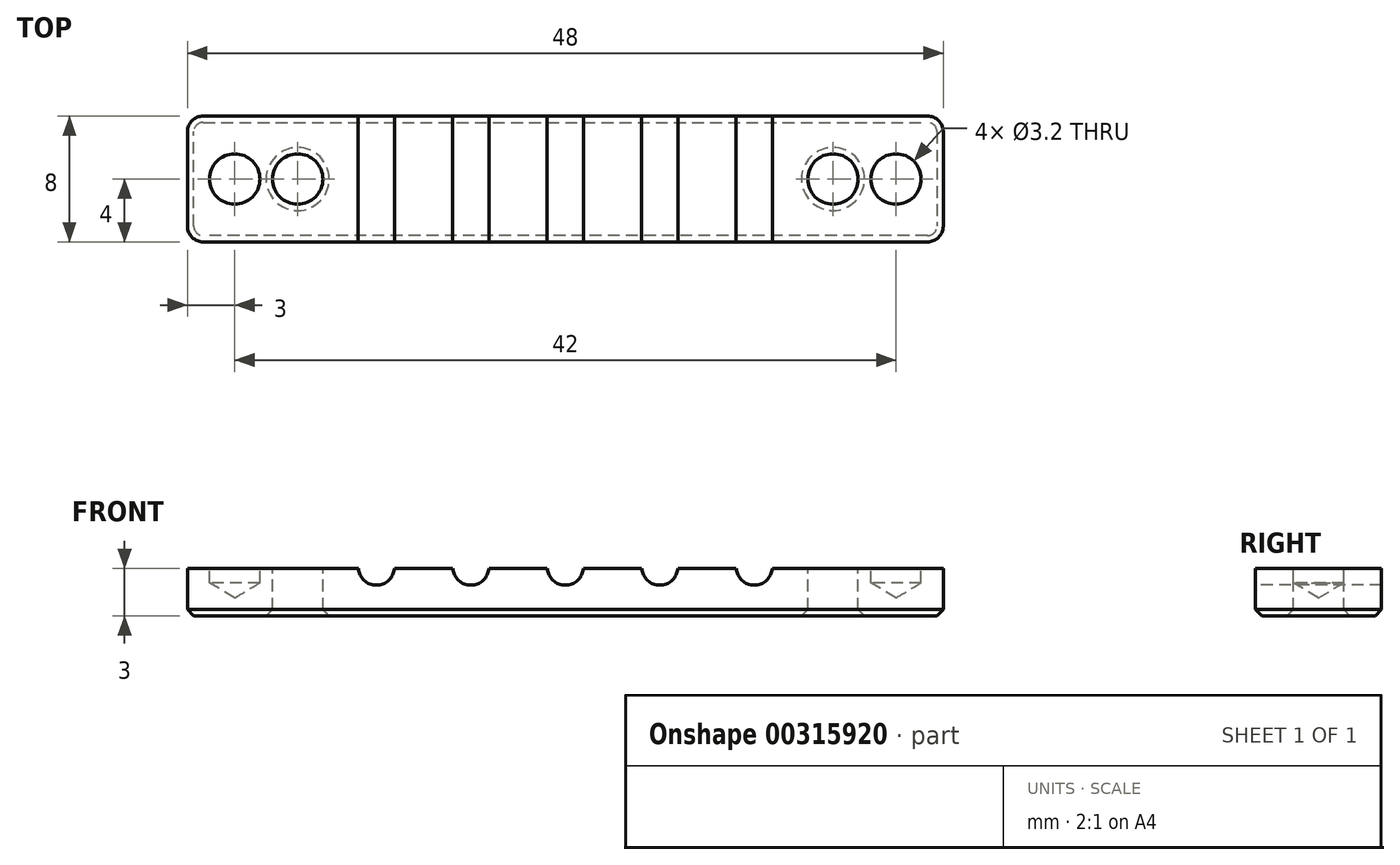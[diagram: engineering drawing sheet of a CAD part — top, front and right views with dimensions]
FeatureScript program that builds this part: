
annotation { "Feature Type Name" : "Feature", "Feature Type Description" : "" }
export const myFeature = defineFeature(function(context is Context, id is Id, definition is map)
    precondition{}
    {
        {
            var Q0;
            Q0=qCreatedBy(makeId("Top.planeOp"),FACE);
            var sketch = newSketch(context, id + "F0", { "sketchPlane" : qUnion([Q0])});
            skLineSegment(sketch, "E0.bottom", {"start": v(3, 4) * mm, "end": v(-3, 4) * mm});
            skLineSegment(sketch, "E0.top", {"start": v(3, -4) * mm, "end": v(-3, -4) * mm});
            skLineSegment(sketch, "E0.left", {"start": v(3, 4) * mm, "end": v(3, -4) * mm});
            skLineSegment(sketch, "E0.right", {"start": v(-3, 4) * mm, "end": v(-3, -4) * mm});
            skPoint(sketch, "E0.middle", {"position": v(0, 0) * mm});
            skLineSegment(sketch, "E1.bottom", {"start": v(45, 4) * mm, "end": v(39, 4) * mm});
            skLineSegment(sketch, "E1.top", {"start": v(45, -4) * mm, "end": v(39, -4) * mm});
            skLineSegment(sketch, "E1.left", {"start": v(45, 4) * mm, "end": v(45, -4) * mm});
            skLineSegment(sketch, "E1.right", {"start": v(39, 4) * mm, "end": v(39, -4) * mm});
            skPoint(sketch, "E1.middle", {"position": v(42, 0) * mm});
            skLineSegment(sketch, "E2", {"start": v(3, 4) * mm, "end": v(39, 4) * mm});
            skLineSegment(sketch, "E3", {"start": v(3, -4) * mm, "end": v(39, -4) * mm});
            skLineSegment(sketch, "E4", {"start": v(9, 4) * mm, "end": v(9, -4) * mm, "construction": true});
            skLineSegment(sketch, "E5.direction1", {"start": v(9, -4) * mm, "end": v(15, -4) * mm, "construction": true});
            skPoint(sketch, "E6", {"position": v(4, 0) * mm});
            skPoint(sketch, "E6.positionSnap0", {"position": v(3, 0) * mm});
            skPoint(sketch, "E7", {"position": v(38, 0) * mm});
            skPoint(sketch, "E7.positionSnap0", {"position": v(39, 0) * mm});
            skLineSegment(sketch, "E8.0.1.0", {"start": v(15, 4) * mm, "end": v(15, -4) * mm, "construction": true});
            skLineSegment(sketch, "E8.0.2.0", {"start": v(21, 4) * mm, "end": v(21, -4) * mm, "construction": true});
            skLineSegment(sketch, "E8.0.3.0", {"start": v(27, 4) * mm, "end": v(27, -4) * mm, "construction": true});
            skLineSegment(sketch, "E8.0.4.0", {"start": v(33, 4) * mm, "end": v(33, -4) * mm, "construction": true});
            skSolve(sketch);
        }
        {
            var Q0;
            Q0=makeQuery(id+"F0.imprint","IMPRINT",FACE,{"disambiguationData":[TD([[makeQuery(id+"F0.imprint","IMPRINT",EDGE,{"derivedFrom":sQuery(id+"F0.wireOp",EDGE,"E0.bottom")}),1.0]])]});
            var Q1;
            Q1=makeQuery(id+"F0.imprint","IMPRINT",FACE,{"disambiguationData":[TD([[makeQuery(id+"F0.imprint","IMPRINT",EDGE,{"derivedFrom":sQuery(id+"F0.wireOp",EDGE,"E0.left")}),1.0]])]});
            var Q2;
            Q2=makeQuery(id+"F0.imprint","IMPRINT",FACE,{"disambiguationData":[TD([[makeQuery(id+"F0.imprint","IMPRINT",EDGE,{"derivedFrom":sQuery(id+"F0.wireOp",EDGE,"E1.bottom")}),1.0]])]});
            extrude(context, id + "F1", {"entities" : qUnion([Q0, Q1, Q2]), "oppositeDirection" : true, "depth" : 3.1 * mm});
        }
        {
            var Q0;
            Q0=sQuery(id+"F0.wireOp",VERTEX,"E6");
            var Q1;
            Q1=sQuery(id+"F0.wireOp",VERTEX,"E7");
            var Q2;
            Q2=makeQuery(id+"F1.opExtrude","SWEPT_BODY",BODY,{"disambiguationData":[OSD([sQuery(id+"F0.wireOp",EDGE,"E0.bottom"),sQuery(id+"F0.wireOp",EDGE,"E0.top"),sQuery(id+"F0.wireOp",EDGE,"E0.right"),sQuery(id+"F0.wireOp",EDGE,"E1.bottom"),sQuery(id+"F0.wireOp",EDGE,"E1.top"),sQuery(id+"F0.wireOp",EDGE,"E1.left"),sQuery(id+"F0.wireOp",EDGE,"E2"),sQuery(id+"F0.wireOp",EDGE,"E3")])]});
            hole(context, id + "F2", {"style" : HoleStyle.SIMPLE, "endStyle" : HoleEndStyle.THROUGH, "holeDiameter" : 3.2 * mm, "tappedDepth" : 12 * mm, "tapClearance" : 3, "locations" : qUnion([Q0, Q1]), "scope" : qUnion([Q2])});
        }
        {
            var Q0;
            Q0=sQuery(id+"F0.wireOp",VERTEX,"E0.middle");
            var Q1;
            Q1=sQuery(id+"F0.wireOp",VERTEX,"E1.middle");
            var Q2;
            Q2=makeQuery(id+"F1.opExtrude","SWEPT_BODY",BODY,{"disambiguationData":[OSD([sQuery(id+"F0.wireOp",EDGE,"E0.bottom"),sQuery(id+"F0.wireOp",EDGE,"E0.top"),sQuery(id+"F0.wireOp",EDGE,"E0.right"),sQuery(id+"F0.wireOp",EDGE,"E1.bottom"),sQuery(id+"F0.wireOp",EDGE,"E1.top"),sQuery(id+"F0.wireOp",EDGE,"E1.left"),sQuery(id+"F0.wireOp",EDGE,"E2"),sQuery(id+"F0.wireOp",EDGE,"E3")])]});
            hole(context, id + "F3", {"style" : HoleStyle.SIMPLE, "endStyle" : HoleEndStyle.BLIND, "holeDiameter" : 3.2 * mm, "holeDepth" : 1 * mm, "tappedDepth" : 12 * mm, "tapClearance" : 3, "locations" : qUnion([Q0, Q1]), "scope" : qUnion([Q2])});
        }
        {
            var Q0;
            {var subQ0=sQuery(id+"F0.wireOp",EDGE,"E3");var subQ1=sQuery(id+"F0.wireOp",EDGE,"E1.top");var subQ2=sQuery(id+"F0.wireOp",EDGE,"E0.top");Q0=makeQuery(id+"FaaVOSY5iOmgxNq_1.boolean.opBoolean","MERGE",FACE,{"derivedFrom":[makeQuery(id+"F1.opExtrude","SWEPT_FACE",FACE,{"disambiguationData":[OSD([subQ2,subQ1,subQ0])]}),makeQuery(id+"FaaVOSY5iOmgxNq_1.opExtrude","SWEPT_FACE",FACE,{"disambiguationData":[OSD([subQ2,subQ1,subQ0])]})]});}
            var sketch = newSketch(context, id + "F4", { "sketchPlane" : qUnion([Q0])});
            skPoint(sketch, "E9", {"position": v(9, 0) * mm});
            skPoint(sketch, "E10.1.0.0", {"position": v(15, 0) * mm});
            skLineSegment(sketch, "E10.direction1", {"start": v(9, 0) * mm, "end": v(15, 0) * mm, "construction": true});
            skPoint(sketch, "E11.0.2.0", {"position": v(21, 0) * mm});
            skPoint(sketch, "E11.0.3.0", {"position": v(27, 0) * mm});
            skPoint(sketch, "E11.0.4.0", {"position": v(33, 0) * mm});
            skSolve(sketch);
        }
        {
            var Q0;
            Q0=sQuery(id+"F4.wireOp",VERTEX,"E9");
            var Q1;
            Q1=sQuery(id+"F4.wireOp",VERTEX,"E10.1.0.0");
            var Q2;
            Q2=sQuery(id+"F4.wireOp",VERTEX,"E11.0.2.0");
            var Q3;
            Q3=sQuery(id+"F4.wireOp",VERTEX,"E11.0.3.0");
            var Q4;
            Q4=sQuery(id+"F4.wireOp",VERTEX,"E11.0.4.0");
            var Q5;
            Q5=makeQuery(id+"F1.opExtrude","SWEPT_BODY",BODY,{"disambiguationData":[OSD([sQuery(id+"F0.wireOp",EDGE,"E0.bottom"),sQuery(id+"F0.wireOp",EDGE,"E0.top"),sQuery(id+"F0.wireOp",EDGE,"E0.right"),sQuery(id+"F0.wireOp",EDGE,"E1.bottom"),sQuery(id+"F0.wireOp",EDGE,"E1.top"),sQuery(id+"F0.wireOp",EDGE,"E1.left"),sQuery(id+"F0.wireOp",EDGE,"E2"),sQuery(id+"F0.wireOp",EDGE,"E3")])]});
            hole(context, id + "F5", {"style" : HoleStyle.SIMPLE, "endStyle" : HoleEndStyle.THROUGH, "holeDiameter" : 2.3 * mm, "tappedDepth" : 12 * mm, "tapClearance" : 3, "locations" : qUnion([Q0, Q1, Q2, Q3, Q4]), "scope" : qUnion([Q5])});
        }
        {
            var Q0;
            Q0=makeQuery(id+"F1.opExtrude","SWEPT_EDGE",EDGE,{"disambiguationData":[OSD([sQuery(id+"F0.wireOp",EDGE,"E0.top"),sQuery(id+"F0.wireOp",EDGE,"E0.right")])]});
            var Q1;
            Q1=makeQuery(id+"F1.opExtrude","SWEPT_EDGE",EDGE,{"disambiguationData":[OSD([sQuery(id+"F0.wireOp",EDGE,"E1.top"),sQuery(id+"F0.wireOp",EDGE,"E1.left")])]});
            var Q2;
            Q2=makeQuery(id+"F1.opExtrude","SWEPT_EDGE",EDGE,{"disambiguationData":[OSD([sQuery(id+"F0.wireOp",EDGE,"E1.bottom"),sQuery(id+"F0.wireOp",EDGE,"E1.left")])]});
            var Q3;
            Q3=makeQuery(id+"F1.opExtrude","SWEPT_EDGE",EDGE,{"disambiguationData":[OSD([sQuery(id+"F0.wireOp",EDGE,"E0.bottom"),sQuery(id+"F0.wireOp",EDGE,"E0.right")])]});
            fillet(context, id + "F6", {"entities" : qUnion([Q0, Q1, Q2, Q3]), "radius" : 1 * mm, "tangentPropagation" : true, "allowEdgeOverflow" : false});
        }
        {
            var Q0;
            Q0=makeQuery(id+"F1.opExtrude","CAP_FACE",FACE,{"disambiguationData":[OSD([sQuery(id+"F0.wireOp",EDGE,"E0.bottom"),sQuery(id+"F0.wireOp",EDGE,"E0.top"),sQuery(id+"F0.wireOp",EDGE,"E0.right"),sQuery(id+"F0.wireOp",EDGE,"E1.bottom"),sQuery(id+"F0.wireOp",EDGE,"E1.top"),sQuery(id+"F0.wireOp",EDGE,"E1.left"),sQuery(id+"F0.wireOp",EDGE,"E2"),sQuery(id+"F0.wireOp",EDGE,"E3")])],"isStart":false});
            chamfer(context, id + "F7", {"entities" : qUnion([Q0]), "width" : 0.4 * mm, "tangentPropagation" : true});
        }
        {
            var Q0;
            {var subQ0=sQuery(id+"F0.wireOp",EDGE,"E0.right");var subQ1=sQuery(id+"F0.wireOp",EDGE,"E3");var subQ2=sQuery(id+"F0.wireOp",EDGE,"E1.top");var subQ3=sQuery(id+"F0.wireOp",EDGE,"E0.top");var subQ4=sQuery(id+"F0.wireOp",EDGE,"E2");var subQ5=sQuery(id+"F0.wireOp",EDGE,"E1.bottom");var subQ6=sQuery(id+"F0.wireOp",EDGE,"E0.bottom");Q0=makeQuery(id+"F5.hole-0.boolean.opBoolean","SPLIT",FACE,{"disambiguationData":[TD([makeQuery(id+"F1.opExtrude","SWEPT_FACE",FACE,{"disambiguationData":[OSD([subQ0])]})])],"derivedFrom":makeQuery(id+"F1.opExtrude","CAP_FACE",FACE,{"disambiguationData":[OSD([subQ6,subQ3,subQ0,subQ5,subQ2,sQuery(id+"F0.wireOp",EDGE,"E1.left"),subQ4,subQ1])],"isStart":true})});}
            var Q1;
            {var subQ0=sQuery(id+"F0.wireOp",EDGE,"E2");var subQ1=sQuery(id+"F0.wireOp",EDGE,"E1.bottom");var subQ2=sQuery(id+"F0.wireOp",EDGE,"E0.bottom");var subQ4=sQuery(id+"F0.wireOp",EDGE,"E3");var subQ5=sQuery(id+"F0.wireOp",EDGE,"E1.top");var subQ6=sQuery(id+"F0.wireOp",EDGE,"E0.top");var subQ8=makeQuery(id+"F5.hole-0.opRevolve","SWEPT_FACE",FACE,{"disambiguationData":[OSD([sQuery(id+"F5.hole-0.sketch.wireOp",EDGE,"core_line_2")])]});var subQ9=makeQuery(id+"F5.hole-0.boolean.opBoolean","COPY",FACE,{"derivedFrom":subQ8});var subQ10=sQuery(id+"F0.wireOp",EDGE,"E1.left");Q1=makeQuery(id+"F5.hole-2.boolean.opBoolean","SPLIT",FACE,{"disambiguationData":[TD([subQ9])],"derivedFrom":makeQuery(id+"F5.hole-1.boolean.opBoolean","SPLIT",FACE,{"disambiguationData":[TD([subQ9])],"derivedFrom":makeQuery(id+"F5.hole-0.boolean.opBoolean","SPLIT",FACE,{"disambiguationData":[TD([makeQuery(id+"F1.opExtrude","SWEPT_FACE",FACE,{"disambiguationData":[OSD([subQ10])]})])],"derivedFrom":makeQuery(id+"F1.opExtrude","CAP_FACE",FACE,{"disambiguationData":[OSD([subQ2,subQ6,sQuery(id+"F0.wireOp",EDGE,"E0.right"),subQ1,subQ5,subQ10,subQ0,subQ4])],"isStart":true})})})});}
            var Q2;
            {var subQ0=sQuery(id+"F0.wireOp",EDGE,"E2");var subQ1=sQuery(id+"F0.wireOp",EDGE,"E1.bottom");var subQ2=sQuery(id+"F0.wireOp",EDGE,"E0.bottom");var subQ4=sQuery(id+"F0.wireOp",EDGE,"E3");var subQ5=sQuery(id+"F0.wireOp",EDGE,"E1.top");var subQ6=sQuery(id+"F0.wireOp",EDGE,"E0.top");var subQ8=makeQuery(id+"F5.hole-1.opRevolve","SWEPT_FACE",FACE,{"disambiguationData":[OSD([sQuery(id+"F5.hole-1.sketch.wireOp",EDGE,"core_line_2")])]});var subQ9=makeQuery(id+"F5.hole-0.opRevolve","SWEPT_FACE",FACE,{"disambiguationData":[OSD([sQuery(id+"F5.hole-0.sketch.wireOp",EDGE,"core_line_2")])]});var subQ10=sQuery(id+"F0.wireOp",EDGE,"E1.left");Q2=makeQuery(id+"F5.hole-2.boolean.opBoolean","SPLIT",FACE,{"disambiguationData":[TD([makeQuery(id+"F5.hole-1.boolean.opBoolean","COPY",FACE,{"derivedFrom":subQ8})])],"derivedFrom":makeQuery(id+"F5.hole-1.boolean.opBoolean","SPLIT",FACE,{"disambiguationData":[TD([makeQuery(id+"F5.hole-0.boolean.opBoolean","COPY",FACE,{"derivedFrom":subQ9})])],"derivedFrom":makeQuery(id+"F5.hole-0.boolean.opBoolean","SPLIT",FACE,{"disambiguationData":[TD([makeQuery(id+"F1.opExtrude","SWEPT_FACE",FACE,{"disambiguationData":[OSD([subQ10])]})])],"derivedFrom":makeQuery(id+"F1.opExtrude","CAP_FACE",FACE,{"disambiguationData":[OSD([subQ2,subQ6,sQuery(id+"F0.wireOp",EDGE,"E0.right"),subQ1,subQ5,subQ10,subQ0,subQ4])],"isStart":true})})})});}
            var Q3;
            {var subQ1=sQuery(id+"F0.wireOp",EDGE,"E3");var subQ2=sQuery(id+"F0.wireOp",EDGE,"E1.top");var subQ3=sQuery(id+"F0.wireOp",EDGE,"E0.top");var subQ5=sQuery(id+"F0.wireOp",EDGE,"E1.left");var subQ6=makeQuery(id+"F1.opExtrude","SWEPT_FACE",FACE,{"disambiguationData":[OSD([subQ5])]});var subQ7=sQuery(id+"F0.wireOp",EDGE,"E2");var subQ8=sQuery(id+"F0.wireOp",EDGE,"E1.bottom");var subQ9=sQuery(id+"F0.wireOp",EDGE,"E0.bottom");Q3=makeQuery(id+"F5.hole-1.boolean.opBoolean","SPLIT",FACE,{"disambiguationData":[TD([subQ6])],"derivedFrom":makeQuery(id+"F5.hole-0.boolean.opBoolean","SPLIT",FACE,{"disambiguationData":[TD([subQ6])],"derivedFrom":makeQuery(id+"F1.opExtrude","CAP_FACE",FACE,{"disambiguationData":[OSD([subQ9,subQ3,sQuery(id+"F0.wireOp",EDGE,"E0.right"),subQ8,subQ2,subQ5,subQ7,subQ1])],"isStart":true})})});}
            extrude(context, id + "F8", {"entities" : qUnion([Q0, Q1, Q2, Q3]), "operationType" : NewBodyOperationType.REMOVE, "oppositeDirection" : true, "depth" : 0.1 * mm});
        }
    });
